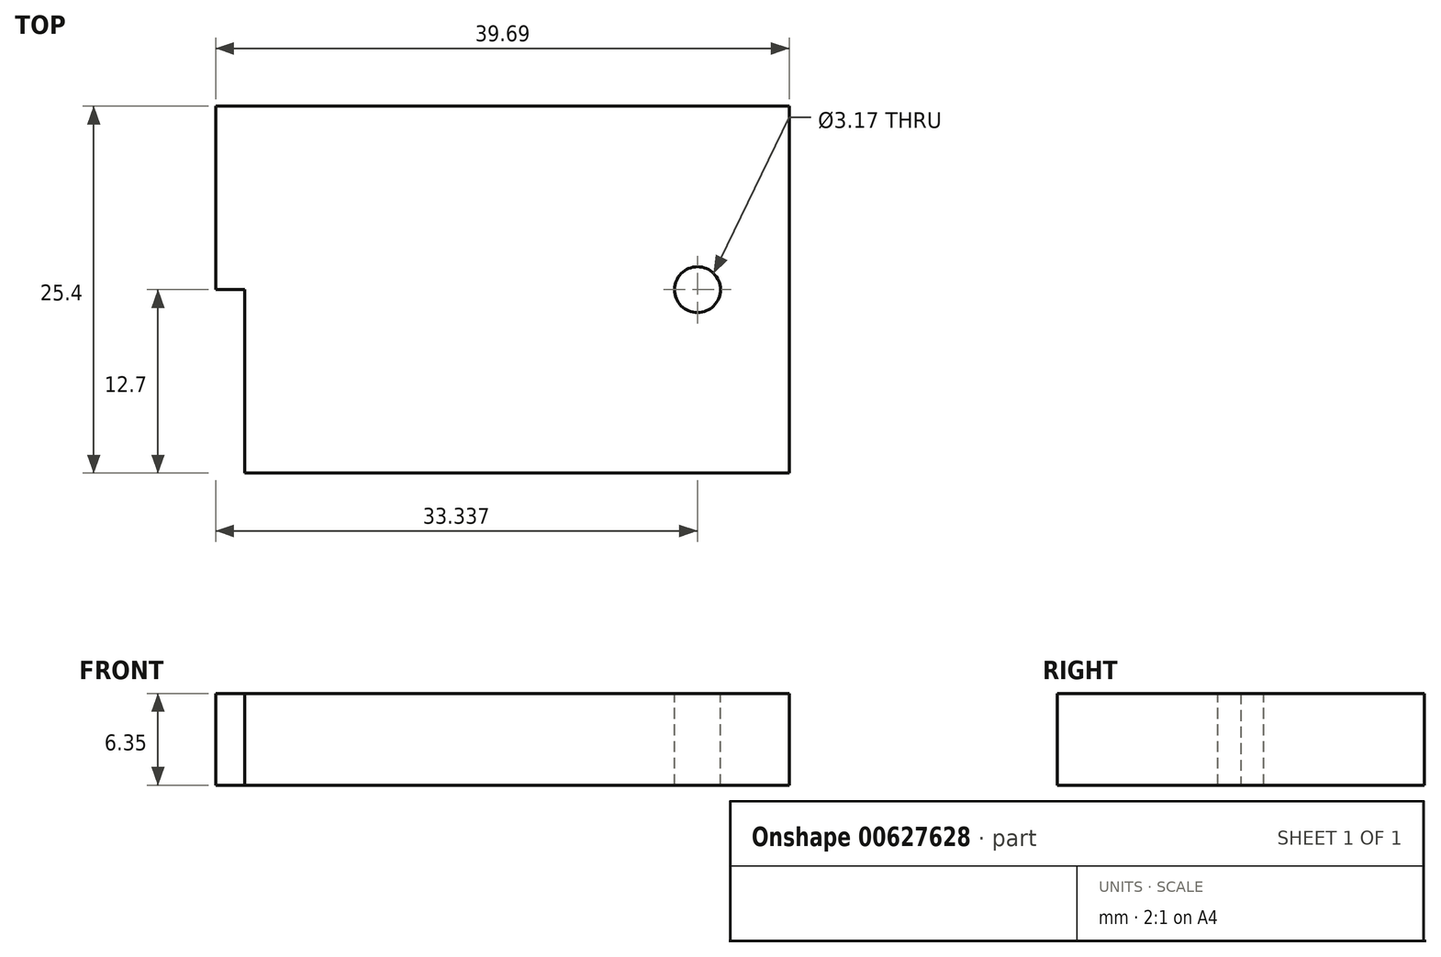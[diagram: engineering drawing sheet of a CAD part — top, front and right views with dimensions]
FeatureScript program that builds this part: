
annotation { "Feature Type Name" : "Feature", "Feature Type Description" : "" }
export const myFeature = defineFeature(function(context is Context, id is Id, definition is map)
    precondition{}
    {
        {
            var Q0;
            Q0=qCreatedBy(makeId("Top.planeOp"),FACE);
            var sketch = newSketch(context, id + "F0", { "sketchPlane" : qUnion([Q0])});
            skLineSegment(sketch, "E0.bottom", {"start": v(0, 0) * mm, "end": v(39.69, 0) * mm});
            skLineSegment(sketch, "E0.top", {"start": v(0, 25.4) * mm, "end": v(39.69, 25.4) * mm});
            skLineSegment(sketch, "E0.left", {"start": v(0, 0) * mm, "end": v(0, 25.4) * mm});
            skLineSegment(sketch, "E0.right", {"start": v(39.69, 0) * mm, "end": v(39.69, 25.4) * mm});
            skSolve(sketch);
        }
        {
            var Q0;
            Q0 = qSketchRegion(id + "F0", true);
            extrude(context, id + "F1", {"entities" : qUnion([Q0]), "depth" : 6.35 * mm, "offsetDistance" : 25.4 * mm});
        }
        {
            var Q0;
            Q0=makeQuery(id+"F1.opExtrude","SWEPT_FACE",FACE,{"disambiguationData":[OSD([sQuery(id+"F0.wireOp",EDGE,"E0.left")])]});
            var sketch = newSketch(context, id + "F2", { "sketchPlane" : qUnion([Q0])});
            skLineSegment(sketch, "E1.bottom", {"start": v(0, 6.35) * mm, "end": v(-12.7, 6.35) * mm});
            skLineSegment(sketch, "E1.top", {"start": v(0, 0) * mm, "end": v(-12.7, 0) * mm});
            skLineSegment(sketch, "E1.left", {"start": v(0, 6.35) * mm, "end": v(0, 0) * mm});
            skLineSegment(sketch, "E1.right", {"start": v(-12.7, 6.35) * mm, "end": v(-12.7, 0) * mm});
            skSolve(sketch);
        }
        {
            var Q0;
            Q0 = qSketchRegion(id + "F2", true);
            extrude(context, id + "F3", {"entities" : qUnion([Q0]), "operationType" : NewBodyOperationType.REMOVE, "oppositeDirection" : true, "depth" : 2 * mm, "offsetDistance" : 25.4 * mm});
        }
        {
            var Q0;
            Q0=makeQuery(id+"F1.opExtrude","CAP_FACE",FACE,{"disambiguationData":[OSD([sQuery(id+"F0.wireOp",EDGE,"E0.bottom"),sQuery(id+"F0.wireOp",EDGE,"E0.top"),sQuery(id+"F0.wireOp",EDGE,"E0.left"),sQuery(id+"F0.wireOp",EDGE,"E0.right")])],"isStart":false});
            var sketch = newSketch(context, id + "F4", { "sketchPlane" : qUnion([Q0])});
            skLineSegment(sketch, "E2", {"start": v(39.69, 12.7) * mm, "end": v(33.34, 12.7) * mm, "construction": true});
            skPoint(sketch, "E2.endSnap0", {"position": v(39.69, 12.7) * mm});
            skCircle(sketch, "E3", {"center": v(33.34, 12.7) * mm, "radius": 1.59 * mm});
            skSolve(sketch);
        }
        {
            var Q0;
            Q0 = qSketchRegion(id + "F4", true);
            extrude(context, id + "F5", {"entities" : qUnion([Q0]), "operationType" : NewBodyOperationType.REMOVE, "oppositeDirection" : true, "depth" : 25.4 * mm, "offsetDistance" : 25.4 * mm});
        }
    });
